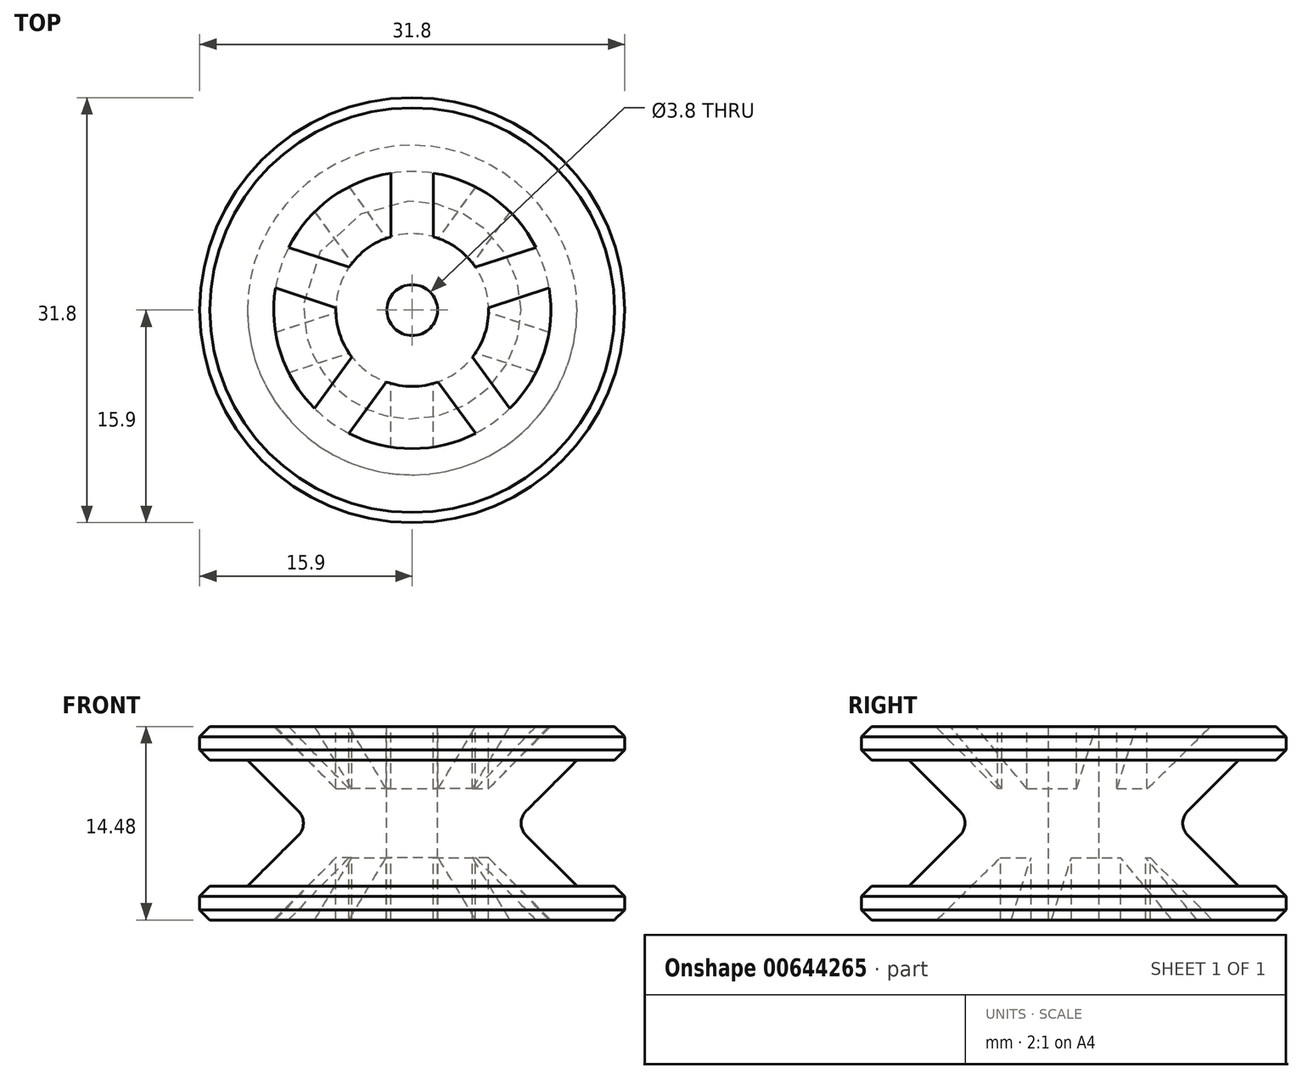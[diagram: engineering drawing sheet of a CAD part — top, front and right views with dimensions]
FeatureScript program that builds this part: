
annotation { "Feature Type Name" : "Feature", "Feature Type Description" : "" }
export const myFeature = defineFeature(function(context is Context, id is Id, definition is map)
    precondition{}
    {
        {
            var Q0;
            Q0=qCreatedBy(makeId("Top.planeOp"),FACE);
            var sketch = newSketch(context, id + "F0", { "sketchPlane" : qUnion([Q0])});
            skCircle(sketch, "E0", {"center": v(0, 0) * mm, "radius": 15.9 * mm});
            skSolve(sketch);
        }
        {
            var Q0;
            Q0 = qSketchRegion(id + "F0", true);
            extrude(context, id + "F1", {"entities" : qUnion([Q0]), "depth" : 14.48 * mm, "offsetDistance" : 25.4 * mm, "symmetric" : true});
        }
        {
            var Q0;
            Q0=makeQuery(id+"F1.opExtrude","CAP_FACE",FACE,{"disambiguationData":[OSD([sQuery(id+"F0.wireOp",EDGE,"E0")])],"isStart":false});
            var sketch = newSketch(context, id + "F2", { "sketchPlane" : qUnion([Q0])});
            skCircle(sketch, "E1", {"center": v(0, 0) * mm, "radius": 1.9 * mm});
            skSolve(sketch);
        }
        {
            var Q0;
            Q0 = qSketchRegion(id + "F2", true);
            extrude(context, id + "F3", {"entities" : qUnion([Q0]), "operationType" : NewBodyOperationType.REMOVE, "endBound" : BoundingType.THROUGH_ALL, "oppositeDirection" : true, "depth" : 25.4 * mm, "offsetDistance" : 25.4 * mm});
        }
        {
            var Q0;
            Q0=qCreatedBy(makeId("Right.planeOp"),FACE);
            var sketch = newSketch(context, id + "F4", { "sketchPlane" : qUnion([Q0])});
            skLineSegment(sketch, "E2", {"start": v(17.74, 4.71) * mm, "end": v(12.33, 4.71) * mm});
            skLineSegment(sketch, "E3", {"start": v(12.33, 4.71) * mm, "end": v(7.62, 0) * mm});
            skLineSegment(sketch, "E4", {"start": v(7.62, 0) * mm, "end": v(12.33, -4.71) * mm});
            skLineSegment(sketch, "E5", {"start": v(12.33, -4.71) * mm, "end": v(17.74, -4.71) * mm});
            skLineSegment(sketch, "E6", {"start": v(17.74, -4.71) * mm, "end": v(17.74, 4.71) * mm});
            skLineSegment(sketch, "E7", {"start": v(0, 0) * mm, "end": v(0, 13.82) * mm, "construction": true});
            skLineSegment(sketch, "E8", {"start": v(5.71, 8.83) * mm, "end": v(5.72, 2.59) * mm});
            skLineSegment(sketch, "E9", {"start": v(5.72, 2.59) * mm, "end": v(11.96, 8.83) * mm});
            skLineSegment(sketch, "E10", {"start": v(11.96, 8.83) * mm, "end": v(5.71, 8.83) * mm});
            skLineSegment(sketch, "E11", {"start": v(0, 0) * mm, "end": v(21.93, 0) * mm, "construction": true});
            skLineSegment(sketch, "E12.MirrorCS", {"start": v(5.71, -8.83) * mm, "end": v(5.72, -2.59) * mm});
            skLineSegment(sketch, "E13.MirrorCS", {"start": v(5.72, -2.59) * mm, "end": v(11.96, -8.83) * mm});
            skLineSegment(sketch, "E14.MirrorCS", {"start": v(11.96, -8.83) * mm, "end": v(5.71, -8.83) * mm});
            skSolve(sketch);
        }
        {
            var Q0;
            Q0 = qSketchRegion(id + "F4", true);
            var Q1;
            Q1=sQuery(id+"F4.wireOp",EDGE,"E7");
            revolve(context, id + "F5", {"operationType" : NewBodyOperationType.REMOVE, "entities" : qUnion([Q0]), "axis" : qUnion([Q1]), "revolveType" : RevolveType.FULL, "oppositeDirection" : true});
        }
        {
            var Q0;
            {var subQ0=sQuery(id+"F0.wireOp",EDGE,"E0");Q0=makeQuery(id+"F5.boolean.opBoolean","SPLIT",FACE,{"disambiguationData":[TD([makeQuery(id+"F1.opExtrude","SWEPT_FACE",FACE,{"disambiguationData":[OSD([subQ0])]})])],"derivedFrom":makeQuery(id+"F1.opExtrude","CAP_FACE",FACE,{"disambiguationData":[OSD([subQ0])],"isStart":false})});}
            var sketch = newSketch(context, id + "F6", { "sketchPlane" : qUnion([Q0])});
            skLineSegment(sketch, "E15.bottom", {"start": v(-1.59, 12.5) * mm, "end": v(1.59, 12.5) * mm});
            skLineSegment(sketch, "E15.top", {"start": v(-1.59, 4.89) * mm, "end": v(1.59, 4.89) * mm});
            skLineSegment(sketch, "E15.left", {"start": v(-1.59, 12.5) * mm, "end": v(-1.59, 4.89) * mm});
            skLineSegment(sketch, "E15.right", {"start": v(1.59, 12.5) * mm, "end": v(1.59, 4.89) * mm});
            skPoint(sketch, "E15.middle", {"position": v(0, 8.7) * mm});
            skLineSegment(sketch, "E16.1.0", {"start": v(-12.38, 2.35) * mm, "end": v(-5.14, 0) * mm});
            skLineSegment(sketch, "E16.1.1", {"start": v(-12.38, 2.35) * mm, "end": v(-11.4, 5.37) * mm});
            skLineSegment(sketch, "E16.1.2", {"start": v(-11.4, 5.37) * mm, "end": v(-4.16, 3.02) * mm});
            skLineSegment(sketch, "E16.1.3", {"start": v(-5.14, 0) * mm, "end": v(-4.16, 3.02) * mm});
            skLineSegment(sketch, "E16.2.0", {"start": v(-6.07, -11.05) * mm, "end": v(-1.59, -4.89) * mm});
            skLineSegment(sketch, "E16.2.1", {"start": v(-6.07, -11.05) * mm, "end": v(-8.64, -9.18) * mm});
            skLineSegment(sketch, "E16.2.2", {"start": v(-8.64, -9.18) * mm, "end": v(-4.16, -3.02) * mm});
            skLineSegment(sketch, "E16.2.3", {"start": v(-1.59, -4.89) * mm, "end": v(-4.16, -3.02) * mm});
            skPoint(sketch, "E16.center", {"position": v(0, 0) * mm});
            skLineSegment(sketch, "E17.2.3.0", {"start": v(8.64, -9.18) * mm, "end": v(4.16, -3.02) * mm});
            skLineSegment(sketch, "E17.3.3.0", {"start": v(8.64, -9.18) * mm, "end": v(6.07, -11.05) * mm});
            skLineSegment(sketch, "E17.6.3.0", {"start": v(6.07, -11.05) * mm, "end": v(1.59, -4.89) * mm});
            skLineSegment(sketch, "E17.9.3.0", {"start": v(4.16, -3.02) * mm, "end": v(1.59, -4.89) * mm});
            skLineSegment(sketch, "E17.2.4.0", {"start": v(11.4, 5.37) * mm, "end": v(4.16, 3.02) * mm});
            skLineSegment(sketch, "E17.3.4.0", {"start": v(11.4, 5.37) * mm, "end": v(12.38, 2.35) * mm});
            skLineSegment(sketch, "E17.6.4.0", {"start": v(12.38, 2.35) * mm, "end": v(5.14, 0) * mm});
            skLineSegment(sketch, "E17.9.4.0", {"start": v(4.16, 3.02) * mm, "end": v(5.14, 0) * mm});
            skSolve(sketch);
        }
        {
            var Q0;
            Q0 = qSketchRegion(id + "F6", true);
            var Q1;
            Q1=makeQuery(id+"F5.boolean.opBoolean","COPY",FACE,{"derivedFrom":makeQuery(id+"F5.opRevolve","SWEPT_FACE",FACE,{"disambiguationData":[OSD([sQuery(id+"F4.wireOp",EDGE,"E9")])]})});
            var Q2;
            Q2=makeQuery(id+"F1.opExtrude","SWEPT_BODY",BODY,{"disambiguationData":[OSD([sQuery(id+"F0.wireOp",EDGE,"E0")])]});
            extrude(context, id + "F7", {"entities" : qUnion([Q0]), "operationType" : NewBodyOperationType.ADD, "endBound" : BoundingType.UP_TO_SURFACE, "oppositeDirection" : true, "depth" : 25.4 * mm, "endBoundEntityFace" : qUnion([Q1]), "endBoundEntityBody" : qUnion([Q2]), "offsetDistance" : 25.4 * mm});
        }
        {
            var Q0;
            Q0=makeQuery(id+"F5.boolean.opBoolean","COPY",EDGE,{"derivedFrom":makeQuery(id+"F5.opRevolve","SWEPT_EDGE",EDGE,{"disambiguationData":[OSD([sQuery(id+"F4.wireOp",EDGE,"E3"),sQuery(id+"F4.wireOp",EDGE,"E4")])]})});
            fillet(context, id + "F8", {"entities" : qUnion([Q0]), "radius" : 1.27 * mm, "tangentPropagation" : true, "allowEdgeOverflow" : false});
        }
        {
            var Q0;
            Q0=makeQuery(id+"F1.opExtrude","CAP_EDGE",EDGE,{"disambiguationData":[OSD([sQuery(id+"F0.wireOp",EDGE,"E0")])],"isStart":false});
            var Q1;
            Q1=makeQuery(id+"F5.boolean.opBoolean","INTERSECT",EDGE,{"derivedFrom":[makeQuery(id+"F1.opExtrude","SWEPT_FACE",FACE,{"disambiguationData":[OSD([sQuery(id+"F0.wireOp",EDGE,"E0")])]}),makeQuery(id+"F5.opRevolve","SWEPT_FACE",FACE,{"disambiguationData":[OSD([sQuery(id+"F4.wireOp",EDGE,"E2")])]})]});
            var Q2;
            Q2=makeQuery(id+"F5.boolean.opBoolean","INTERSECT",EDGE,{"derivedFrom":[makeQuery(id+"F1.opExtrude","SWEPT_FACE",FACE,{"disambiguationData":[OSD([sQuery(id+"F0.wireOp",EDGE,"E0")])]}),makeQuery(id+"F5.opRevolve","SWEPT_FACE",FACE,{"disambiguationData":[OSD([sQuery(id+"F4.wireOp",EDGE,"E5")])]})]});
            var Q3;
            Q3=makeQuery(id+"F1.opExtrude","CAP_EDGE",EDGE,{"disambiguationData":[OSD([sQuery(id+"F0.wireOp",EDGE,"E0")])],"isStart":true});
            chamfer(context, id + "F9", {"entities" : qUnion([Q0, Q1, Q2, Q3]), "width" : 0.76 * mm, "tangentPropagation" : true});
        }
        {
            var Q0;
            {var subQ0=sQuery(id+"F0.wireOp",EDGE,"E0");Q0=makeQuery(id+"F5.boolean.opBoolean","SPLIT",FACE,{"disambiguationData":[TD([makeQuery(id+"F1.opExtrude","SWEPT_FACE",FACE,{"disambiguationData":[OSD([subQ0])]})])],"derivedFrom":makeQuery(id+"F1.opExtrude","CAP_FACE",FACE,{"disambiguationData":[OSD([subQ0])],"isStart":true})});}
            var sketch = newSketch(context, id + "F10", { "sketchPlane" : qUnion([Q0])});
            skLineSegment(sketch, "E18.bottom", {"start": v(1.59, 11.62) * mm, "end": v(-1.59, 11.62) * mm});
            skLineSegment(sketch, "E18.top", {"start": v(1.59, 4.6) * mm, "end": v(-1.59, 4.6) * mm});
            skLineSegment(sketch, "E18.left", {"start": v(1.59, 11.62) * mm, "end": v(1.59, 4.6) * mm});
            skLineSegment(sketch, "E18.right", {"start": v(-1.59, 11.62) * mm, "end": v(-1.59, 4.6) * mm});
            skPoint(sketch, "E19", {"position": v(0, 4.6) * mm});
            skPoint(sketch, "E20.1.0", {"position": v(-4.37, 1.42) * mm});
            skLineSegment(sketch, "E20.1.1", {"start": v(-10.56, 5.1) * mm, "end": v(-11.54, 2.08) * mm});
            skLineSegment(sketch, "E20.1.2", {"start": v(-3.88, 2.93) * mm, "end": v(-4.87, -0.09) * mm});
            skLineSegment(sketch, "E20.1.3", {"start": v(-10.56, 5.1) * mm, "end": v(-3.88, 2.93) * mm});
            skLineSegment(sketch, "E20.1.4", {"start": v(-11.54, 2.08) * mm, "end": v(-4.87, -0.09) * mm});
            skPoint(sketch, "E20.2.0", {"position": v(-2.7, -3.72) * mm});
            skLineSegment(sketch, "E20.2.1", {"start": v(-8.12, -8.47) * mm, "end": v(-5.55, -10.33) * mm});
            skLineSegment(sketch, "E20.2.2", {"start": v(-3.99, -2.79) * mm, "end": v(-1.42, -4.65) * mm});
            skLineSegment(sketch, "E20.2.3", {"start": v(-8.12, -8.47) * mm, "end": v(-3.99, -2.79) * mm});
            skLineSegment(sketch, "E20.2.4", {"start": v(-5.55, -10.33) * mm, "end": v(-1.42, -4.65) * mm});
            skPoint(sketch, "E20.center", {"position": v(0, 0) * mm});
            skLineSegment(sketch, "E21.1.3.0", {"start": v(5.55, -10.33) * mm, "end": v(8.12, -8.47) * mm});
            skLineSegment(sketch, "E21.4.3.0", {"start": v(1.42, -4.65) * mm, "end": v(3.99, -2.79) * mm});
            skPoint(sketch, "E21.6.3.0", {"position": v(2.7, -3.72) * mm});
            skLineSegment(sketch, "E21.7.3.0", {"start": v(5.55, -10.33) * mm, "end": v(1.42, -4.65) * mm});
            skLineSegment(sketch, "E21.10.3.0", {"start": v(8.12, -8.47) * mm, "end": v(3.99, -2.79) * mm});
            skLineSegment(sketch, "E21.1.4.0", {"start": v(11.54, 2.08) * mm, "end": v(10.56, 5.1) * mm});
            skLineSegment(sketch, "E21.4.4.0", {"start": v(4.87, -0.09) * mm, "end": v(3.88, 2.93) * mm});
            skPoint(sketch, "E21.6.4.0", {"position": v(4.37, 1.42) * mm});
            skLineSegment(sketch, "E21.7.4.0", {"start": v(11.54, 2.08) * mm, "end": v(4.87, -0.09) * mm});
            skLineSegment(sketch, "E21.10.4.0", {"start": v(10.56, 5.1) * mm, "end": v(3.88, 2.93) * mm});
            skSolve(sketch);
        }
        {
            var Q0;
            Q0 = qSketchRegion(id + "F10", true);
            var Q1;
            Q1=makeQuery(id+"F5.boolean.opBoolean","COPY",FACE,{"derivedFrom":makeQuery(id+"F5.opRevolve","SWEPT_FACE",FACE,{"disambiguationData":[OSD([sQuery(id+"F4.wireOp",EDGE,"E13.MirrorCS")])]})});
            extrude(context, id + "F11", {"entities" : qUnion([Q0]), "operationType" : NewBodyOperationType.ADD, "endBound" : BoundingType.UP_TO_SURFACE, "oppositeDirection" : true, "depth" : 25.4 * mm, "endBoundEntityFace" : qUnion([Q1]), "offsetDistance" : 25.4 * mm});
        }
    });
